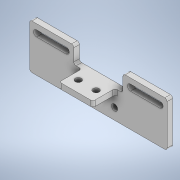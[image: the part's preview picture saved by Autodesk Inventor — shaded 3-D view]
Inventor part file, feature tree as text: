
AUTODESK INVENTOR PART (.ipt)
format: ipt  version: 2021.4 (Build 254397000, 397)  size: 192,512 bytes
history: native  units: mm
features: sketch x7, extrude x4, hole x2, other x1, fillet x1
ambient origin geometry x8: Origin, YZ Plane, XZ Plane, XY Plane, X Axis, Y Axis, Z Axis, Center Point
bodies: Body1 (feature_tree)
feature tree (15):
  other  "ソリッド1"
  extrude  "押し出し1"  Depth=123.0mm
  extrude  "押し出し2"  Depth=40.0mm
  extrude  "押し出し3"  Depth=5.0mm TaperAngle=0.0deg
  hole  "穴1"  [1 undecoded]
  extrude  "押し出し4"  Depth=15.0mm
  sketch  "スケッチ6"
  hole  "穴2"  [1 undecoded]
  fillet  "フィレット1"  Radius=5.0mm
  sketch  "スケッチ1"
  sketch  "スケッチ2"
  sketch  "スケッチ3"
  sketch  "スケッチ4"
  sketch  "スケッチ5"
  sketch  "スケッチ7"
note: 2 required parameter values undecoded (feature->parameter linkage not recoverable at this tier; creation-order binding heuristic only, values carry confidence <= 0.55)
